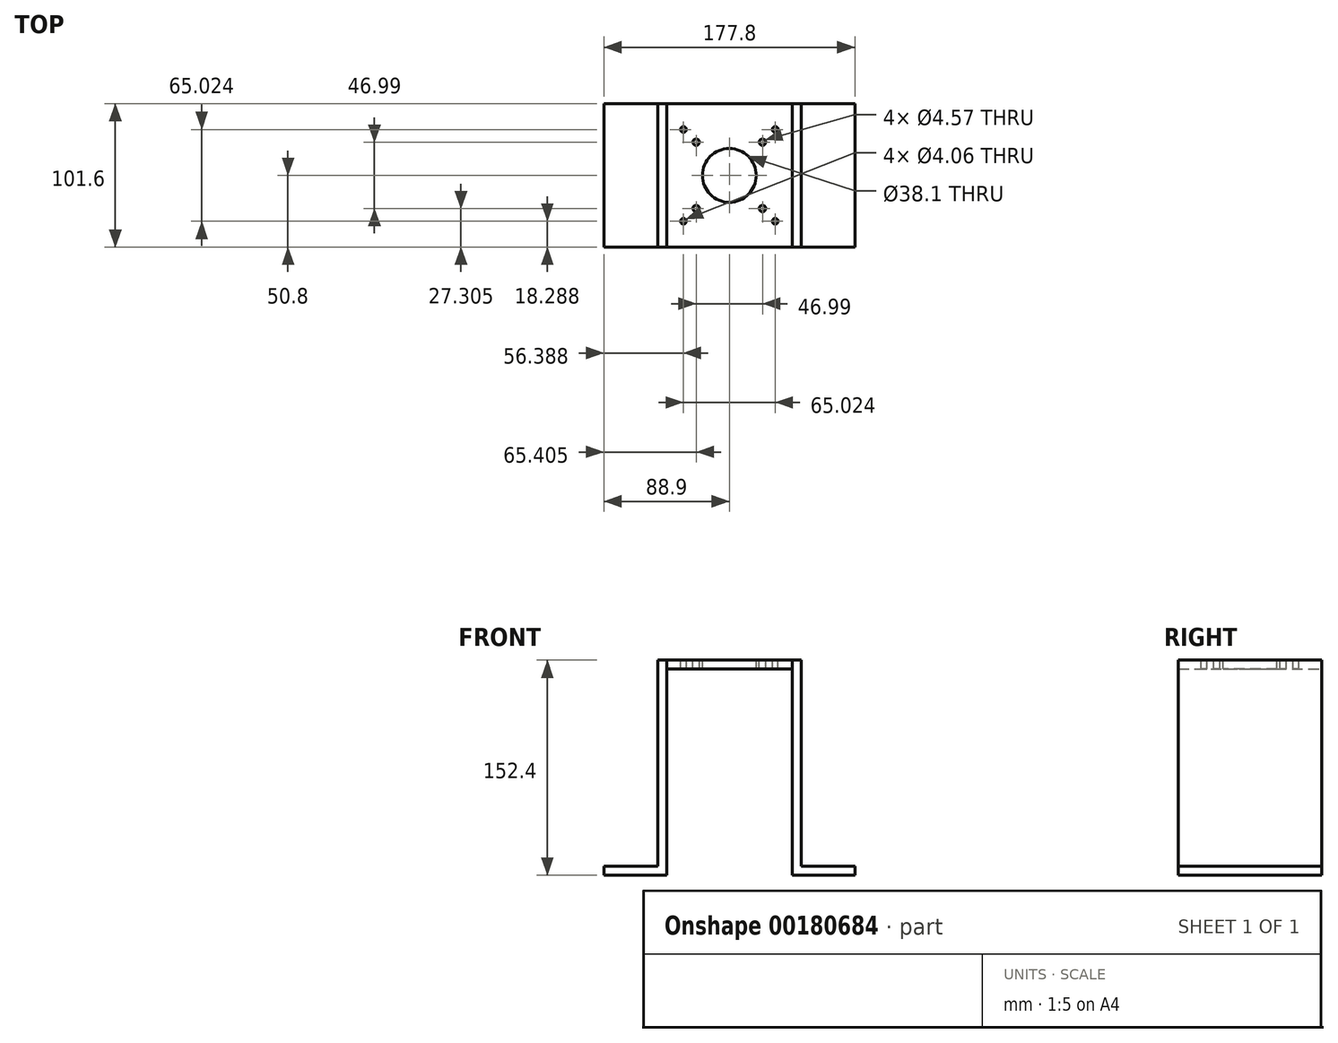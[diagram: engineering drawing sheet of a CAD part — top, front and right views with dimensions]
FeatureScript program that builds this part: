
annotation { "Feature Type Name" : "Feature", "Feature Type Description" : "" }
export const myFeature = defineFeature(function(context is Context, id is Id, definition is map)
    precondition{}
    {
        {
            var Q0;
            Q0=qCreatedBy(makeId("Top.planeOp"),FACE);
            cPlane(context, id + "F0", {"entities" : qUnion([Q0]), "cplaneType" : CPlaneType.OFFSET, "offset" : 152.4 * mm, "width" : 152.4 * mm, "height" : 152.4 * mm});
        }
        {
            var Q0;
            Q0=qCreatedBy(id+"F0.planeOp",FACE);
            var sketch = newSketch(context, id + "F1", { "sketchPlane" : qUnion([Q0])});
            skLineSegment(sketch, "E0.bottom", {"start": v(50.8, 50.8) * mm, "end": v(-50.8, 50.8) * mm});
            skLineSegment(sketch, "E0.top", {"start": v(50.8, -50.8) * mm, "end": v(-50.8, -50.8) * mm});
            skLineSegment(sketch, "E0.left", {"start": v(50.8, 50.8) * mm, "end": v(50.8, -50.8) * mm});
            skLineSegment(sketch, "E0.right", {"start": v(-50.8, 50.8) * mm, "end": v(-50.8, -50.8) * mm});
            skPoint(sketch, "E0.middle", {"position": v(0, 0) * mm});
            skLineSegment(sketch, "E1", {"start": v(-44.45, 50.8) * mm, "end": v(-44.45, -50.8) * mm});
            skLineSegment(sketch, "E2", {"start": v(44.45, -50.8) * mm, "end": v(44.45, 50.8) * mm});
            skCircle(sketch, "E3", {"center": v(0, 0) * mm, "radius": 19.05 * mm});
            skCircle(sketch, "E4", {"center": v(-23.5, 23.5) * mm, "radius": 2.29 * mm});
            skCircle(sketch, "E5.0.1.0", {"center": v(-23.5, -23.5) * mm, "radius": 2.29 * mm});
            skCircle(sketch, "E5.1.0.0", {"center": v(23.5, 23.5) * mm, "radius": 2.29 * mm});
            skCircle(sketch, "E5.1.1.0", {"center": v(23.5, -23.5) * mm, "radius": 2.29 * mm});
            skLineSegment(sketch, "E5.direction1", {"start": v(-23.5, 23.5) * mm, "end": v(23.5, 23.5) * mm, "construction": true});
            skLineSegment(sketch, "E5.direction2", {"start": v(-23.5, 23.5) * mm, "end": v(-23.5, -23.5) * mm, "construction": true});
            skCircle(sketch, "E6", {"center": v(-32.51, 32.51) * mm, "radius": 2.03 * mm});
            skCircle(sketch, "E7.0.1.0", {"center": v(-32.51, -32.51) * mm, "radius": 2.03 * mm});
            skCircle(sketch, "E7.1.0.0", {"center": v(32.51, 32.51) * mm, "radius": 2.03 * mm});
            skCircle(sketch, "E7.1.1.0", {"center": v(32.51, -32.51) * mm, "radius": 2.03 * mm});
            skLineSegment(sketch, "E7.direction1", {"start": v(-32.51, 32.51) * mm, "end": v(32.51, 32.51) * mm, "construction": true});
            skLineSegment(sketch, "E7.direction2", {"start": v(-32.51, 32.51) * mm, "end": v(-32.51, -32.51) * mm, "construction": true});
            skSolve(sketch);
        }
        {
            var Q0;
            {var subQ0=sQuery(id+"F1.wireOp",EDGE,"E1");Q0=makeQuery(id+"F1.imprint","IMPRINT",FACE,{"disambiguationData":[TD([[makeQuery(id+"F1.imprint","IMPRINT",EDGE,{"derivedFrom":subQ0}),1.0]])]});}
            extrude(context, id + "F2", {"entities" : qUnion([Q0]), "oppositeDirection" : true, "depth" : 6.35 * mm});
        }
        {
            var Q0;
            {var subQ0=sQuery(id+"F1.wireOp",EDGE,"E0.right");Q0=makeQuery(id+"F1.imprint","IMPRINT",FACE,{"disambiguationData":[TD([[makeQuery(id+"F1.imprint","IMPRINT",EDGE,{"derivedFrom":subQ0}),1.0]])]});}
            var Q1;
            {var subQ0=sQuery(id+"F1.wireOp",EDGE,"E0.left");Q1=makeQuery(id+"F1.imprint","IMPRINT",FACE,{"disambiguationData":[TD([[makeQuery(id+"F1.imprint","IMPRINT",EDGE,{"derivedFrom":subQ0}),-1.0]])]});}
            extrude(context, id + "F3", {"entities" : qUnion([Q0, Q1]), "oppositeDirection" : true, "depth" : 152.4 * mm});
        }
        {
            var Q0;
            Q0=makeQuery(id+"F3.opExtrude","SWEPT_FACE",FACE,{"disambiguationData":[OSD([sQuery(id+"F1.wireOp",EDGE,"E0.left")])]});
            var sketch = newSketch(context, id + "F4", { "sketchPlane" : qUnion([Q0])});
            skLineSegment(sketch, "E8", {"start": v(-50.8, 6.35) * mm, "end": v(50.8, 6.35) * mm});
            skSolve(sketch);
        }
        {
            var Q0;
            {var subQ0=sQuery(id+"F4.wireOp",EDGE,"E8");Q0=makeQuery(id+"F4.imprint","IMPRINT",FACE,{"disambiguationData":[TD([[makeQuery(id+"F4.imprint","IMPRINT",EDGE,{"derivedFrom":subQ0}),-1.0]])]});}
            extrude(context, id + "F5", {"entities" : qUnion([Q0]), "operationType" : NewBodyOperationType.ADD, "depth" : 38.1 * mm});
        }
        {
            var Q0;
            Q0=makeQuery(id+"F3.opExtrude","SWEPT_FACE",FACE,{"disambiguationData":[OSD([sQuery(id+"F1.wireOp",EDGE,"E0.right")])]});
            var sketch = newSketch(context, id + "F6", { "sketchPlane" : qUnion([Q0])});
            skLineSegment(sketch, "E9", {"start": v(-50.8, 6.35) * mm, "end": v(50.8, 6.35) * mm});
            skSolve(sketch);
        }
        {
            var Q0;
            {var subQ0=sQuery(id+"F6.wireOp",EDGE,"E9");Q0=makeQuery(id+"F6.imprint","IMPRINT",FACE,{"disambiguationData":[TD([[makeQuery(id+"F6.imprint","IMPRINT",EDGE,{"derivedFrom":subQ0}),-1.0]])]});}
            extrude(context, id + "F7", {"entities" : qUnion([Q0]), "operationType" : NewBodyOperationType.ADD, "depth" : 38.1 * mm});
        }
    });
